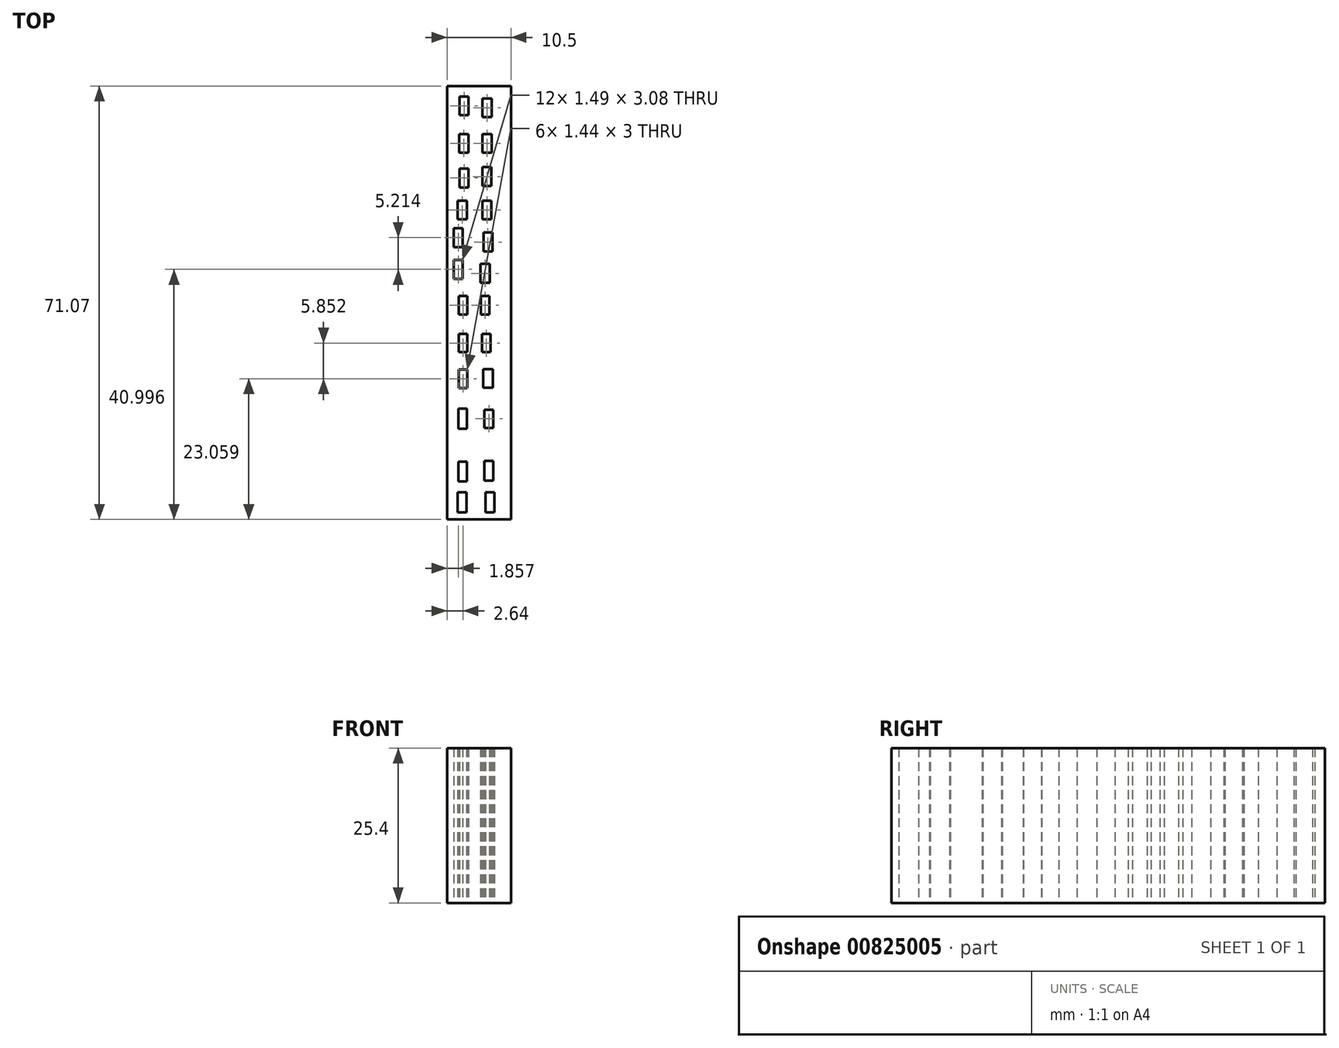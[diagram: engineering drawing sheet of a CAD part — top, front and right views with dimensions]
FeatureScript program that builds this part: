
annotation { "Feature Type Name" : "Feature", "Feature Type Description" : "" }
export const myFeature = defineFeature(function(context is Context, id is Id, definition is map)
    precondition{}
    {
        {
            var Q0;
            Q0=qCreatedBy(makeId("Top.planeOp"),FACE);
            var sketch = newSketch(context, id + "F0", { "sketchPlane" : qUnion([Q0])});
            skLineSegment(sketch, "E0.bottom", {"start": v(-59.44, 71.07) * mm, "end": v(-48.94, 71.07) * mm});
            skLineSegment(sketch, "E0.top", {"start": v(-59.44, 0) * mm, "end": v(-48.94, 0) * mm});
            skLineSegment(sketch, "E0.left", {"start": v(-59.44, 71.07) * mm, "end": v(-59.44, 0) * mm});
            skLineSegment(sketch, "E0.right", {"start": v(-48.94, 71.07) * mm, "end": v(-48.94, 0) * mm});
            skLineSegment(sketch, "E1.bottom", {"start": v(-57.6, 18.15) * mm, "end": v(-56.15, 18.15) * mm});
            skLineSegment(sketch, "E1.top", {"start": v(-57.6, 14.87) * mm, "end": v(-56.15, 14.87) * mm});
            skLineSegment(sketch, "E1.left", {"start": v(-57.6, 18.15) * mm, "end": v(-57.6, 14.87) * mm});
            skLineSegment(sketch, "E1.right", {"start": v(-56.15, 18.15) * mm, "end": v(-56.15, 14.87) * mm});
            skLineSegment(sketch, "E2.bottom", {"start": v(-57.4, 69.37) * mm, "end": v(-55.9, 69.37) * mm});
            skLineSegment(sketch, "E2.top", {"start": v(-57.4, 66.3) * mm, "end": v(-55.9, 66.3) * mm});
            skLineSegment(sketch, "E2.left", {"start": v(-57.4, 69.37) * mm, "end": v(-57.4, 66.3) * mm});
            skLineSegment(sketch, "E2.right", {"start": v(-55.9, 69.37) * mm, "end": v(-55.9, 66.3) * mm});
            skLineSegment(sketch, "E3.bottom", {"start": v(-53.61, 69.03) * mm, "end": v(-52.13, 69.03) * mm});
            skLineSegment(sketch, "E3.top", {"start": v(-53.61, 65.95) * mm, "end": v(-52.13, 65.95) * mm});
            skLineSegment(sketch, "E3.left", {"start": v(-53.61, 69.03) * mm, "end": v(-53.61, 65.95) * mm});
            skLineSegment(sketch, "E3.right", {"start": v(-52.13, 69.03) * mm, "end": v(-52.13, 65.95) * mm});
            skLineSegment(sketch, "E4.bottom", {"start": v(-57.43, 63.2) * mm, "end": v(-55.94, 63.2) * mm});
            skLineSegment(sketch, "E4.top", {"start": v(-57.43, 60.11) * mm, "end": v(-55.94, 60.11) * mm});
            skLineSegment(sketch, "E4.left", {"start": v(-57.43, 63.2) * mm, "end": v(-57.43, 60.11) * mm});
            skLineSegment(sketch, "E4.right", {"start": v(-55.94, 63.2) * mm, "end": v(-55.94, 60.11) * mm});
            skLineSegment(sketch, "E5.bottom", {"start": v(-53.61, 63.2) * mm, "end": v(-52.13, 63.2) * mm});
            skLineSegment(sketch, "E5.top", {"start": v(-53.61, 60.11) * mm, "end": v(-52.13, 60.11) * mm});
            skLineSegment(sketch, "E5.left", {"start": v(-53.61, 63.2) * mm, "end": v(-53.61, 60.11) * mm});
            skLineSegment(sketch, "E5.right", {"start": v(-52.13, 63.2) * mm, "end": v(-52.13, 60.11) * mm});
            skLineSegment(sketch, "E6.bottom", {"start": v(-57.37, 57.53) * mm, "end": v(-55.89, 57.53) * mm});
            skLineSegment(sketch, "E6.top", {"start": v(-57.37, 54.45) * mm, "end": v(-55.89, 54.45) * mm});
            skLineSegment(sketch, "E6.left", {"start": v(-57.37, 57.53) * mm, "end": v(-57.37, 54.45) * mm});
            skLineSegment(sketch, "E6.right", {"start": v(-55.89, 57.53) * mm, "end": v(-55.89, 54.45) * mm});
            skLineSegment(sketch, "E7.bottom", {"start": v(-53.62, 57.76) * mm, "end": v(-52.14, 57.76) * mm});
            skLineSegment(sketch, "E7.top", {"start": v(-53.62, 54.68) * mm, "end": v(-52.14, 54.68) * mm});
            skLineSegment(sketch, "E7.left", {"start": v(-53.62, 57.76) * mm, "end": v(-53.62, 54.68) * mm});
            skLineSegment(sketch, "E7.right", {"start": v(-52.14, 57.76) * mm, "end": v(-52.14, 54.68) * mm});
            skLineSegment(sketch, "E8.bottom", {"start": v(-57.68, 52.28) * mm, "end": v(-56.2, 52.28) * mm});
            skLineSegment(sketch, "E8.top", {"start": v(-57.68, 49.2) * mm, "end": v(-56.2, 49.2) * mm});
            skLineSegment(sketch, "E8.left", {"start": v(-57.68, 52.28) * mm, "end": v(-57.68, 49.2) * mm});
            skLineSegment(sketch, "E8.right", {"start": v(-56.2, 52.28) * mm, "end": v(-56.2, 49.2) * mm});
            skLineSegment(sketch, "E9.bottom", {"start": v(-53.62, 52.28) * mm, "end": v(-52.14, 52.28) * mm});
            skLineSegment(sketch, "E9.top", {"start": v(-53.62, 49.2) * mm, "end": v(-52.14, 49.2) * mm});
            skLineSegment(sketch, "E9.left", {"start": v(-53.62, 52.28) * mm, "end": v(-53.62, 49.2) * mm});
            skLineSegment(sketch, "E9.right", {"start": v(-52.14, 52.28) * mm, "end": v(-52.14, 49.2) * mm});
            skLineSegment(sketch, "E10.bottom", {"start": v(-58.33, 47.75) * mm, "end": v(-56.84, 47.75) * mm});
            skLineSegment(sketch, "E10.top", {"start": v(-58.33, 44.67) * mm, "end": v(-56.84, 44.67) * mm});
            skLineSegment(sketch, "E10.left", {"start": v(-58.33, 47.75) * mm, "end": v(-58.33, 44.67) * mm});
            skLineSegment(sketch, "E10.right", {"start": v(-56.84, 47.75) * mm, "end": v(-56.84, 44.67) * mm});
            skLineSegment(sketch, "E11.bottom", {"start": v(-53.47, 47.04) * mm, "end": v(-51.98, 47.04) * mm});
            skLineSegment(sketch, "E11.top", {"start": v(-53.47, 43.96) * mm, "end": v(-51.98, 43.96) * mm});
            skLineSegment(sketch, "E11.left", {"start": v(-53.47, 47.04) * mm, "end": v(-53.47, 43.96) * mm});
            skLineSegment(sketch, "E11.right", {"start": v(-51.98, 47.04) * mm, "end": v(-51.98, 43.96) * mm});
            skLineSegment(sketch, "E12.bottom", {"start": v(-58.33, 42.54) * mm, "end": v(-56.84, 42.54) * mm});
            skLineSegment(sketch, "E12.top", {"start": v(-58.33, 39.46) * mm, "end": v(-56.84, 39.46) * mm});
            skLineSegment(sketch, "E12.left", {"start": v(-58.33, 42.54) * mm, "end": v(-58.33, 39.46) * mm});
            skLineSegment(sketch, "E12.right", {"start": v(-56.84, 42.54) * mm, "end": v(-56.84, 39.46) * mm});
            skLineSegment(sketch, "E13.bottom", {"start": v(-53.94, 41.88) * mm, "end": v(-52.46, 41.88) * mm});
            skLineSegment(sketch, "E13.top", {"start": v(-53.94, 38.8) * mm, "end": v(-52.46, 38.8) * mm});
            skLineSegment(sketch, "E13.left", {"start": v(-53.94, 41.88) * mm, "end": v(-53.94, 38.8) * mm});
            skLineSegment(sketch, "E13.right", {"start": v(-52.46, 41.88) * mm, "end": v(-52.46, 38.8) * mm});
            skLineSegment(sketch, "E14.bottom", {"start": v(-57.52, 36.62) * mm, "end": v(-56.08, 36.62) * mm});
            skLineSegment(sketch, "E14.top", {"start": v(-57.52, 33.61) * mm, "end": v(-56.08, 33.61) * mm});
            skLineSegment(sketch, "E14.left", {"start": v(-57.52, 36.62) * mm, "end": v(-57.52, 33.61) * mm});
            skLineSegment(sketch, "E14.right", {"start": v(-56.08, 36.62) * mm, "end": v(-56.08, 33.61) * mm});
            skLineSegment(sketch, "E15.bottom", {"start": v(-53.91, 36.62) * mm, "end": v(-52.47, 36.62) * mm});
            skLineSegment(sketch, "E15.top", {"start": v(-53.91, 33.61) * mm, "end": v(-52.47, 33.61) * mm});
            skLineSegment(sketch, "E15.left", {"start": v(-53.91, 36.62) * mm, "end": v(-53.91, 33.61) * mm});
            skLineSegment(sketch, "E15.right", {"start": v(-52.47, 36.62) * mm, "end": v(-52.47, 33.61) * mm});
            skLineSegment(sketch, "E16.bottom", {"start": v(-57.52, 30.41) * mm, "end": v(-56.08, 30.41) * mm});
            skLineSegment(sketch, "E16.top", {"start": v(-57.52, 27.4) * mm, "end": v(-56.08, 27.4) * mm});
            skLineSegment(sketch, "E16.left", {"start": v(-57.52, 30.41) * mm, "end": v(-57.52, 27.4) * mm});
            skLineSegment(sketch, "E16.right", {"start": v(-56.08, 30.41) * mm, "end": v(-56.08, 27.4) * mm});
            skLineSegment(sketch, "E17.bottom", {"start": v(-53.71, 30.41) * mm, "end": v(-52.27, 30.41) * mm});
            skLineSegment(sketch, "E17.top", {"start": v(-53.71, 27.4) * mm, "end": v(-52.27, 27.4) * mm});
            skLineSegment(sketch, "E17.left", {"start": v(-53.71, 30.41) * mm, "end": v(-53.71, 27.4) * mm});
            skLineSegment(sketch, "E17.right", {"start": v(-52.27, 30.41) * mm, "end": v(-52.27, 27.4) * mm});
            skLineSegment(sketch, "E18.bottom", {"start": v(-57.52, 24.56) * mm, "end": v(-56.08, 24.56) * mm});
            skLineSegment(sketch, "E18.top", {"start": v(-57.52, 24.46) * mm, "end": v(-56.08, 24.46) * mm});
            skLineSegment(sketch, "E18.left", {"start": v(-57.52, 24.56) * mm, "end": v(-57.52, 24.46) * mm});
            skLineSegment(sketch, "E18.right", {"start": v(-56.08, 24.56) * mm, "end": v(-56.08, 24.46) * mm});
            skLineSegment(sketch, "E19.bottom", {"start": v(-56.08, 24.56) * mm, "end": v(-56.08, 24.56) * mm});
            skLineSegment(sketch, "E19.top", {"start": v(-56.08, 21.56) * mm, "end": v(-56.08, 21.56) * mm});
            skLineSegment(sketch, "E19.left", {"start": v(-56.08, 24.56) * mm, "end": v(-56.08, 21.56) * mm});
            skLineSegment(sketch, "E19.right", {"start": v(-56.08, 24.56) * mm, "end": v(-56.08, 21.56) * mm});
            skLineSegment(sketch, "E20.bottom", {"start": v(-57.52, 24.56) * mm, "end": v(-57.52, 24.56) * mm});
            skLineSegment(sketch, "E20.top", {"start": v(-57.52, 21.56) * mm, "end": v(-57.52, 21.56) * mm});
            skLineSegment(sketch, "E20.left", {"start": v(-57.52, 24.56) * mm, "end": v(-57.52, 21.56) * mm});
            skLineSegment(sketch, "E20.right", {"start": v(-57.52, 24.56) * mm, "end": v(-57.52, 21.56) * mm});
            skLineSegment(sketch, "E21.bottom", {"start": v(-57.52, 21.56) * mm, "end": v(-56.08, 21.56) * mm});
            skLineSegment(sketch, "E21.top", {"start": v(-57.52, 21.56) * mm, "end": v(-56.08, 21.56) * mm});
            skLineSegment(sketch, "E22.bottom", {"start": v(-53.47, 24.62) * mm, "end": v(-51.94, 24.62) * mm});
            skLineSegment(sketch, "E22.top", {"start": v(-53.47, 21.62) * mm, "end": v(-51.94, 21.62) * mm});
            skLineSegment(sketch, "E22.left", {"start": v(-53.47, 24.62) * mm, "end": v(-53.47, 21.62) * mm});
            skLineSegment(sketch, "E22.right", {"start": v(-51.94, 24.62) * mm, "end": v(-51.94, 21.62) * mm});
            skLineSegment(sketch, "E23.bottom", {"start": v(-53.3, 18) * mm, "end": v(-51.85, 18) * mm});
            skLineSegment(sketch, "E23.top", {"start": v(-53.3, 15) * mm, "end": v(-51.85, 15) * mm});
            skLineSegment(sketch, "E23.left", {"start": v(-53.3, 18) * mm, "end": v(-53.3, 15) * mm});
            skLineSegment(sketch, "E23.right", {"start": v(-51.85, 18) * mm, "end": v(-51.85, 15) * mm});
            skLineSegment(sketch, "E24.bottom", {"start": v(-57.6, 9.48) * mm, "end": v(-56.15, 9.48) * mm});
            skLineSegment(sketch, "E24.top", {"start": v(-57.6, 6.2) * mm, "end": v(-56.15, 6.2) * mm});
            skLineSegment(sketch, "E24.left", {"start": v(-57.6, 9.48) * mm, "end": v(-57.6, 6.2) * mm});
            skLineSegment(sketch, "E24.right", {"start": v(-56.15, 9.48) * mm, "end": v(-56.15, 6.2) * mm});
            skLineSegment(sketch, "E25.bottom", {"start": v(-53.28, 9.62) * mm, "end": v(-51.84, 9.62) * mm});
            skLineSegment(sketch, "E25.top", {"start": v(-53.28, 6.34) * mm, "end": v(-51.84, 6.34) * mm});
            skLineSegment(sketch, "E25.left", {"start": v(-53.28, 9.62) * mm, "end": v(-53.28, 6.34) * mm});
            skLineSegment(sketch, "E25.right", {"start": v(-51.84, 9.62) * mm, "end": v(-51.84, 6.34) * mm});
            skLineSegment(sketch, "E26.top", {"start": v(-57.75, 0) * mm, "end": v(-55.8, 0) * mm});
            skLineSegment(sketch, "E27.top", {"start": v(-52.58, 0) * mm, "end": v(-50.54, 0) * mm});
            skLineSegment(sketch, "E28.bottom", {"start": v(-56.26, 1.17) * mm, "end": v(-57.7, 1.17) * mm});
            skLineSegment(sketch, "E28.top", {"start": v(-56.26, 4.45) * mm, "end": v(-57.7, 4.45) * mm});
            skLineSegment(sketch, "E28.left", {"start": v(-56.26, 1.17) * mm, "end": v(-56.26, 4.45) * mm});
            skLineSegment(sketch, "E28.right", {"start": v(-57.7, 1.17) * mm, "end": v(-57.7, 4.45) * mm});
            skLineSegment(sketch, "E29.bottom", {"start": v(-53.12, 4.45) * mm, "end": v(-51.67, 4.45) * mm});
            skLineSegment(sketch, "E29.top", {"start": v(-53.12, 1.17) * mm, "end": v(-51.67, 1.17) * mm});
            skLineSegment(sketch, "E29.left", {"start": v(-53.12, 4.45) * mm, "end": v(-53.12, 1.17) * mm});
            skLineSegment(sketch, "E29.right", {"start": v(-51.67, 4.45) * mm, "end": v(-51.67, 1.17) * mm});
            skSolve(sketch);
        }
        {
            var Q0;
            Q0 = qSketchRegion(id + "F0", true);
            extrude(context, id + "F1", {"entities" : qUnion([Q0]), "depth" : 25.4 * mm, "offsetDistance" : 25.4 * mm});
        }
    });
